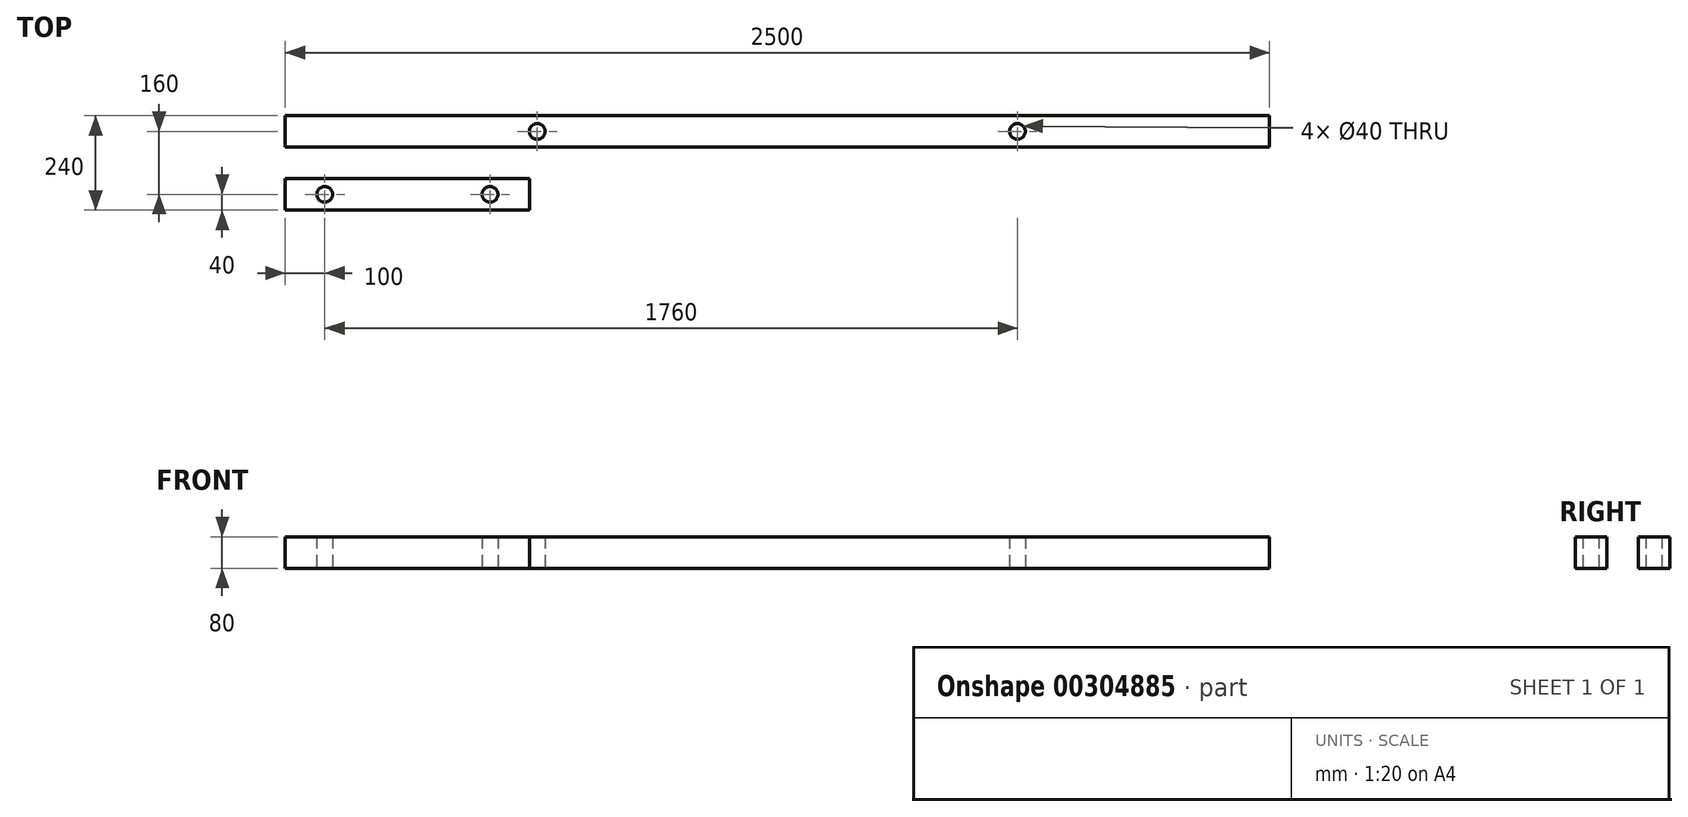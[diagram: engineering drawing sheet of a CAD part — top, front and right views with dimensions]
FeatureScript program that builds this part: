
annotation { "Feature Type Name" : "Feature", "Feature Type Description" : "" }
export const myFeature = defineFeature(function(context is Context, id is Id, definition is map)
    precondition{}
    {
        {
            var Q0;
            Q0=qCreatedBy(makeId("Top.planeOp"),FACE);
            var sketch = newSketch(context, id + "F0", { "sketchPlane" : qUnion([Q0])});
            skLineSegment(sketch, "E0.bottom", {"start": v(0, 0) * mm, "end": v(2500, 0) * mm});
            skLineSegment(sketch, "E0.top", {"start": v(0, 80) * mm, "end": v(2500, 80) * mm});
            skLineSegment(sketch, "E0.left", {"start": v(0, 0) * mm, "end": v(0, 80) * mm});
            skLineSegment(sketch, "E0.right", {"start": v(2500, 0) * mm, "end": v(2500, 80) * mm});
            skLineSegment(sketch, "E1.bottom", {"start": v(0, -80) * mm, "end": v(620, -80) * mm});
            skLineSegment(sketch, "E1.top", {"start": v(0, -160) * mm, "end": v(620, -160) * mm});
            skLineSegment(sketch, "E1.left", {"start": v(0, -80) * mm, "end": v(0, -160) * mm});
            skLineSegment(sketch, "E1.right", {"start": v(620, -80) * mm, "end": v(620, -160) * mm});
            skCircle(sketch, "E2", {"center": v(100, -120) * mm, "radius": 20 * mm});
            skCircle(sketch, "E3", {"center": v(520, -120) * mm, "radius": 20 * mm});
            skCircle(sketch, "E4", {"center": v(640, 40) * mm, "radius": 20 * mm});
            skCircle(sketch, "E5", {"center": v(1860, 40) * mm, "radius": 20 * mm});
            skSolve(sketch);
        }
        {
            var Q0;
            Q0=makeQuery(id+"F0.imprint","IMPRINT",FACE,{"disambiguationData":[TD([[makeQuery(id+"F0.imprint","IMPRINT",EDGE,{"derivedFrom":sQuery(id+"F0.wireOp",EDGE,"E0.bottom")}),1.0]])]});
            var Q1;
            Q1=makeQuery(id+"F0.imprint","IMPRINT",FACE,{"disambiguationData":[TD([[makeQuery(id+"F0.imprint","IMPRINT",EDGE,{"derivedFrom":sQuery(id+"F0.wireOp",EDGE,"E1.bottom")}),-1.0]])]});
            extrude(context, id + "F1", {"entities" : qUnion([Q0, Q1]), "depth" : 80 * mm});
        }
    });
